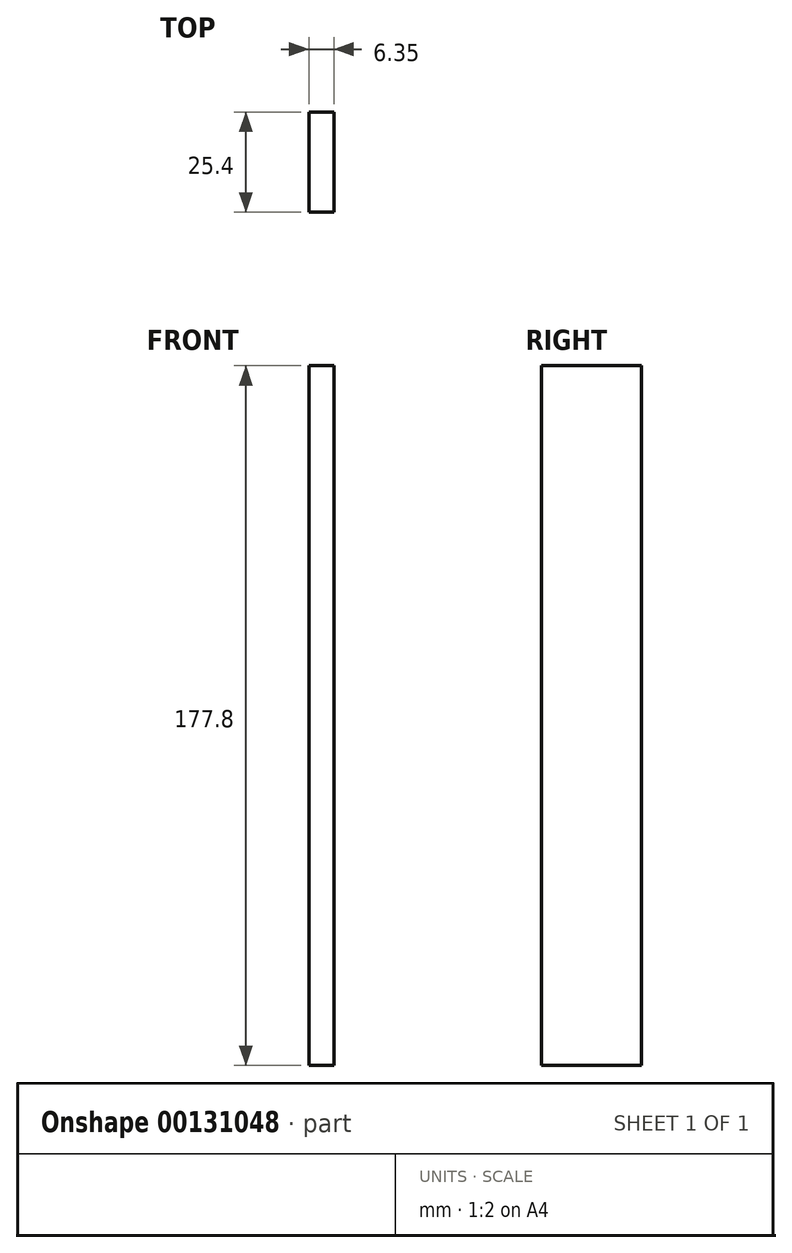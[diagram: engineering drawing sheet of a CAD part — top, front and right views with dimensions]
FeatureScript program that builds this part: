
annotation { "Feature Type Name" : "Feature", "Feature Type Description" : "" }
export const myFeature = defineFeature(function(context is Context, id is Id, definition is map)
    precondition{}
    {
        {
            var Q0;
            Q0=qCreatedBy(makeId("Front.planeOp"),FACE);
            var sketch = newSketch(context, id + "F0", { "sketchPlane" : qUnion([Q0])});
            skLineSegment(sketch, "E0.bottom", {"start": v(-20.54, -51.6) * mm, "end": v(-14.2, -51.6) * mm});
            skLineSegment(sketch, "E0.top", {"start": v(-20.54, 126.2) * mm, "end": v(-14.2, 126.2) * mm});
            skLineSegment(sketch, "E0.left", {"start": v(-20.54, -51.6) * mm, "end": v(-20.54, 126.2) * mm});
            skLineSegment(sketch, "E0.right", {"start": v(-14.2, -51.6) * mm, "end": v(-14.2, 126.2) * mm});
            skSolve(sketch);
        }
        {
            var Q0;
            Q0=makeQuery(id+"F0.imprint","IMPRINT",FACE,{"disambiguationData":[TD([[makeQuery(id+"F0.imprint","IMPRINT",EDGE,{"derivedFrom":sQuery(id+"F0.wireOp",EDGE,"E0.bottom")}),1.0]])]});
            extrude(context, id + "F1", {"entities" : qUnion([Q0]), "depth" : 25.4 * mm});
        }
    });
